FCSTD DOCUMENT  (FreeCAD 0.19R24276 (Git))
Label: MS_1
License: All rights reserved
LicenseURL: http://en.wikipedia.org/wiki/All_rights_reserved
objects: Sketcher::SketchObject×1, PartDesign::Body×1
note: 2 computed .brp shape members not serialized (recipe doc carries the construction recipe); baked Part::Feature solids carry a one-line shape summary decoded from their .brp

FEATURE [Sketcher::SketchObject] Sketch
  FullyConstrained = false
  MapMode = 5
  Support = -> [XY_Plane]
  sketch-geometry (21):
    g0: Circle CenterX=0 CenterY=0 CenterZ=0 NormalX=0 NormalY=0 NormalZ=1 AngleXU=0 Radius=8
    g1: Circle CenterX=30 CenterY=0 CenterZ=0 NormalX=0 NormalY=0 NormalZ=1 AngleXU=0 Radius=11
    g2: LineSegment StartX=30 StartY=0 StartZ=0 EndX=117.724 EndY=-27.7221 EndZ=0
    g3: Circle CenterX=60 CenterY=-30 CenterZ=0 NormalX=0 NormalY=0 NormalZ=1 AngleXU=0 Radius=12
    g4: LineSegment StartX=60 StartY=-30 StartZ=0 EndX=145.644 EndY=-63.6022 EndZ=0
    g5: Circle CenterX=0 CenterY=0 CenterZ=0 NormalX=0 NormalY=0 NormalZ=1 AngleXU=0 Radius=42
    g6: Circle CenterX=0 CenterY=0 CenterZ=0 NormalX=0 NormalY=0 NormalZ=1 AngleXU=0 Radius=56.5
    g7: Circle CenterX=117.724 CenterY=-27.7221 CenterZ=0 NormalX=0 NormalY=0 NormalZ=1 AngleXU=0 Radius=8
    g8: LineSegment StartX=8.13531 StartY=-41.2046 StartZ=0 EndX=116.174 EndY=-19.8737 EndZ=0
    g9: LineSegment StartX=117.724 StartY=-27.7221 StartZ=0 EndX=116.174 EndY=-19.8737 EndZ=0
    g10: LineSegment StartX=8.13531 StartY=-41.2046 StartZ=0 EndX=0 EndY=0 EndZ=0
    g11: LineSegment StartX=18.3743 StartY=-53.4288 StartZ=0 EndX=115.122 EndY=-20.157 EndZ=0
    g12: LineSegment StartX=0 StartY=0 StartZ=0 EndX=18.3743 EndY=-53.4288 EndZ=0
    g13: LineSegment StartX=117.724 StartY=-27.7221 StartZ=0 EndX=115.122 EndY=-20.157 EndZ=0
    g14: Circle CenterX=145.644 CenterY=-63.6022 CenterZ=0 NormalX=0 NormalY=0 NormalZ=1 AngleXU=0 Radius=8
    g15: LineSegment StartX=-3.84548 StartY=-41.8236 StartZ=0 EndX=146.376 EndY=-55.6358 EndZ=0
    g16: LineSegment StartX=145.644 StartY=-63.6022 StartZ=0 EndX=146.376 EndY=-55.6358 EndZ=0
    g17: LineSegment StartX=0 StartY=0 StartZ=0 EndX=-3.84548 EndY=-41.8236 EndZ=0
    g18: LineSegment StartX=0.348764 StartY=-56.4989 StartZ=0 EndX=145.595 EndY=-55.6023 EndZ=0
    g19: LineSegment StartX=145.644 StartY=-63.6022 StartZ=0 EndX=145.595 EndY=-55.6023 EndZ=0
    g20: LineSegment StartX=0 StartY=0 StartZ=0 EndX=0.348764 EndY=-56.4989 EndZ=0
  constraints (52):
    c: Coincident(g0,g-1)
    c: PointOnObject(g1,g-1)
    c: Coincident(g2,g1)
    c: Distance(g2,g1) = 92
    c: DistanceX(g0,g1) = 30
    c: Coincident(g4,g3)
    c: Distance(g4,g3) = 92
    c: DistanceY(g3,g0) = 30
    c: Coincident(g5,g0)
    c: Coincident(g6,g0)
    c: Diameter(g5) = 84
    c: Diameter(g6) = 113
    c: Coincident(g7,g2)
    c: Diameter(g7) = 16
    c: Diameter(g3) = 24
    c: Diameter(g0) = 16
    c: Diameter(g1) = 22
    c: PointOnObject(g8,g5)
    c: PointOnObject(g8,g7)
    c: Coincident(g9,g2)
    c: Coincident(g9,g8)
    c: Perpendicular(g9,g8)
    c: Coincident(g10,g8)
    c: Coincident(g10,g0)
    c: Perpendicular(g8,g10)
    c: PointOnObject(g11,g6)
    c: Coincident(g12,g0)
    c: Coincident(g12,g11)
    c: Perpendicular(g11,g12)
    c: Coincident(g13,g2)
    c: PointOnObject(g13,g7)
    c: Coincident(g11,g13)
    c: Perpendicular(g11,g13)
    c: Coincident(g14,g4)
    c: Equal(g7,g14)
    c: PointOnObject(g15,g5)
    c: PointOnObject(g15,g14)
    c: Tangent(g15,g14)
    c: Coincident(g16,g4)
    c: Coincident(g16,g15)
    c: Coincident(g17,g0)
    c: Coincident(g17,g15)
    c: Perpendicular(g15,g17)
    c: DistanceX(g0,g3) = 60
    c: PointOnObject(g18,g6)
    c: PointOnObject(g18,g14)
    c: Coincident(g19,g4)
    c: Coincident(g19,g18)
    c: Perpendicular(g19,g18)
    c: Coincident(g20,g0)
    c: Coincident(g20,g18)
    c: Perpendicular(g18,g20)
FEATURE [PartDesign::Body] Body
  Group = -> [Sketch]
  Origin = -> Origin
